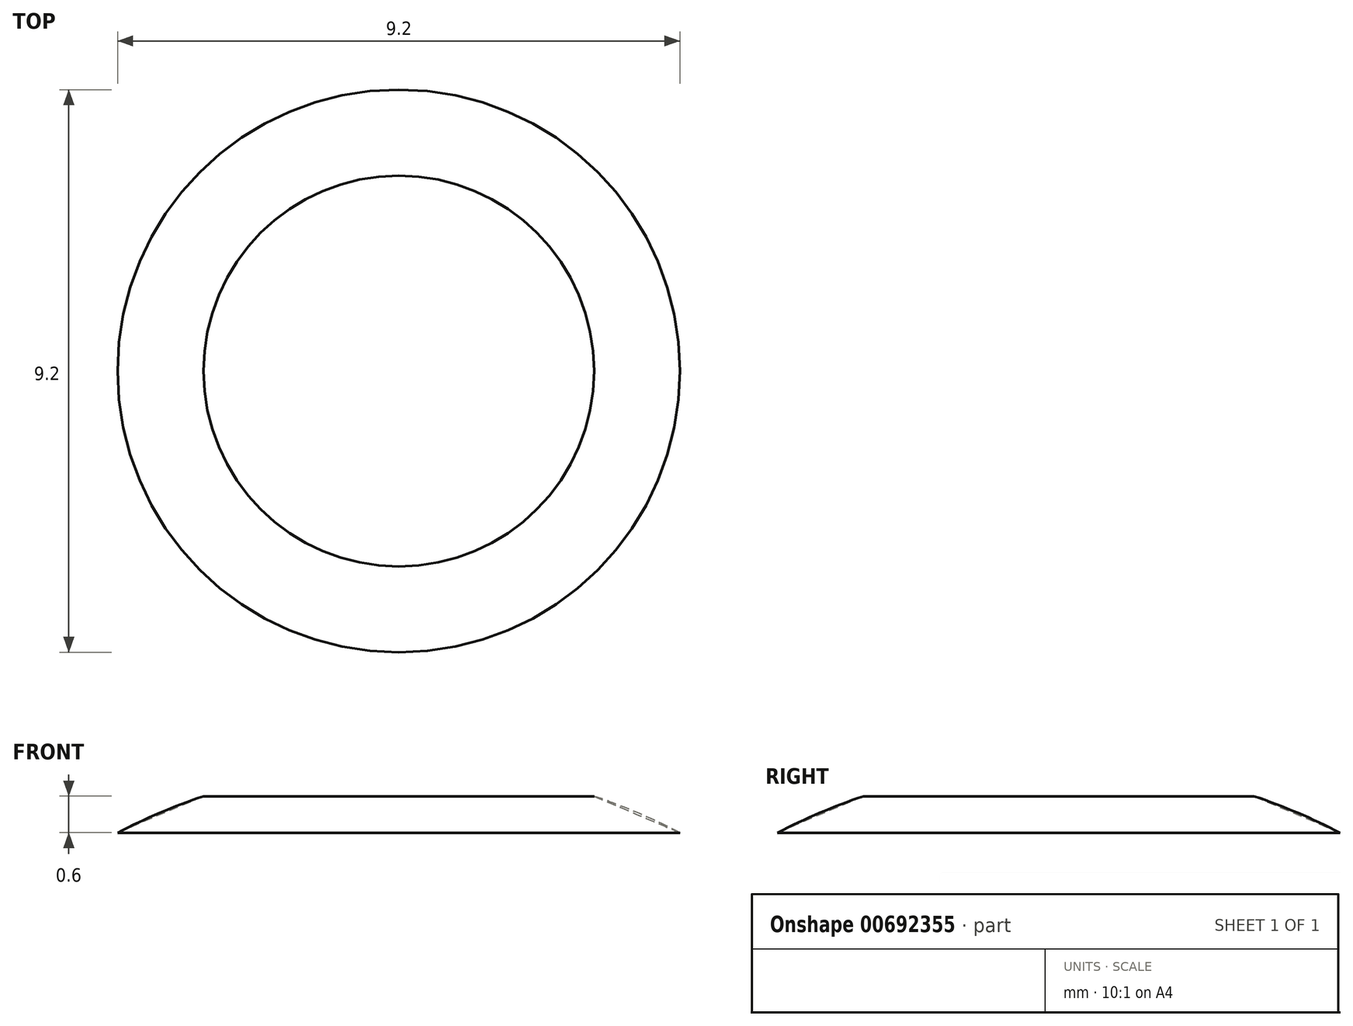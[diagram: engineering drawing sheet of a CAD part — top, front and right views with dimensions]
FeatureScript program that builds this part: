
annotation { "Feature Type Name" : "Feature", "Feature Type Description" : "" }
export const myFeature = defineFeature(function(context is Context, id is Id, definition is map)
    precondition{}
    {
        {
            var Q0;
            Q0=qCreatedBy(makeId("Front.planeOp"),FACE);
            var sketch = newSketch(context, id + "F0", { "sketchPlane" : qUnion([Q0])});
            skLineSegment(sketch, "E0", {"start": v(0, 0) * mm, "end": v(0, 3.3) * mm, "construction": true});
            skArc(sketch, "E1", {"start": v(0, -10) * mm, "mid": v(9.87, -1.62) * mm, "end": v(3.2, 9.48) * mm});
            skLineSegment(sketch, "E2", {"start": v(0, 10.83) * mm, "end": v(4.6, 8.88) * mm});
            skLineSegment(sketch, "E3", {"start": v(0, 0) * mm, "end": v(0, -10) * mm});
            skLineSegment(sketch, "E4", {"start": v(0, 0) * mm, "end": v(0, -3.48) * mm, "construction": true});
            skLineSegment(sketch, "E5", {"start": v(0, 10.83) * mm, "end": v(0, -10) * mm});
            skSolve(sketch);
        }
        {
            var Q0;
            {var subQ0=sQuery(id+"F0.wireOp",EDGE,"E5");var subQ1=sQuery(id+"F0.wireOp",EDGE,"E1");var subQ2=makeQuery(id+"F0.imprint","INTERSECT",VERTEX,{"derivedFrom":[subQ1,subQ0]});Q0=makeQuery(id+"F0.imprint","IMPRINT",FACE,{"disambiguationData":[TD([[makeQuery(id+"F0.imprint","IMPRINT",EDGE,{"disambiguationData":[TD([[subQ2,-1.0]])],"derivedFrom":subQ1}),1.0]])]});}
            var Q1;
            Q1=sQuery(id+"F0.wireOp",EDGE,"E5");
            revolve(context, id + "F1", {"entities" : qUnion([Q0]), "axis" : qUnion([Q1]), "revolveType" : RevolveType.FULL});
        }
    });
